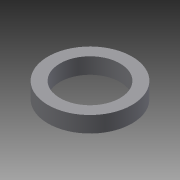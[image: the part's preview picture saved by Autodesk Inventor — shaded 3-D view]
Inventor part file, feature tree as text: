
AUTODESK INVENTOR PART (.ipt)
format: ipt  version: 2013 (Build 170138000, 138)  size: 73,728 bytes
history: native  units: mm
features: extrude x1, sketch x1
ambient origin geometry x8: Origin, YZ Plane, XZ Plane, XY Plane, X Axis, Y Axis, Z Axis, Center Point
bodies: Solid1 (feature_tree)
feature tree (2):
  extrude  "Extrusion1"  Depth=21.0mm
  sketch  "Sketch1"  dims[d0=15.0mm d2=21.0mm d3=4.0mm d4=0.0mm]
